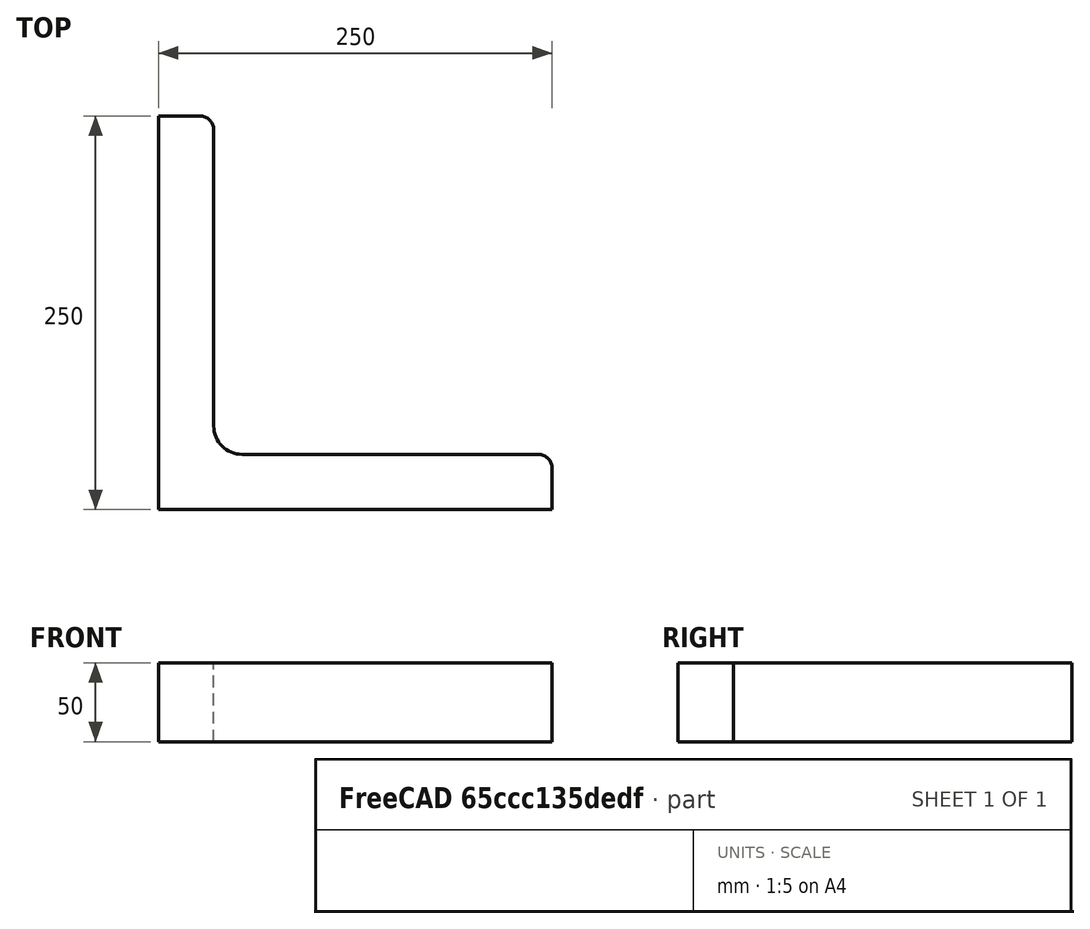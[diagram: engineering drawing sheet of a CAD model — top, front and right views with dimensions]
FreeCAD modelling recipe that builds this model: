
FCSTD DOCUMENT  (FreeCAD 0.15R4671 (Git))
Label: Angle Bar L250x250x35 EN10056 S235JR
License: All rights reserved
LicenseURL: http://en.wikipedia.org/wiki/All_rights_reserved
objects: Sketcher::SketchObject×1, Part::Extrusion×1
note: 2 computed .brp shape members not serialized (recipe doc carries the construction recipe); baked Part::Feature solids carry a one-line shape summary decoded from their .brp

FEATURE [Sketcher::SketchObject] Sketch
  sketch-geometry (9):
    g0: LineSegment StartX=0 StartY=0 StartZ=0 EndX=250 EndY=0 EndZ=0
    g1: LineSegment StartX=250 StartY=0 StartZ=0 EndX=250 EndY=26 EndZ=0
    g2: LineSegment StartX=241 StartY=35 StartZ=0 EndX=53 EndY=35 EndZ=0
    g3: LineSegment StartX=0 StartY=0 StartZ=0 EndX=0 EndY=250 EndZ=0
    g4: LineSegment StartX=0 StartY=250 StartZ=0 EndX=26 EndY=250 EndZ=0
    g5: LineSegment StartX=35 StartY=241 StartZ=0 EndX=35 EndY=53 EndZ=0
    g6: ArcOfCircle CenterX=53 CenterY=53 CenterZ=0 NormalX=0 NormalY=0 NormalZ=1 Radius=18 StartAngle=3.14159 EndAngle=4.71239
    g7: ArcOfCircle CenterX=26 CenterY=241 CenterZ=0 NormalX=0 NormalY=0 NormalZ=1 Radius=9 StartAngle=0 EndAngle=1.5708
    g8: ArcOfCircle CenterX=241 CenterY=26 CenterZ=0 NormalX=0 NormalY=0 NormalZ=1 Radius=9 StartAngle=0 EndAngle=1.5708
  constraints (23):
    c: Coincident(g0,g-1)
    c: Horizontal(g0)
    c: Coincident(g1,g0)
    c: Vertical(g1)
    c: Horizontal(g2)
    c: Coincident(g3,g-1)
    c: Vertical(g3)
    c: Coincident(g4,g3)
    c: Horizontal(g4)
    c: Vertical(g5)
    c: Tangent(g5,g6) = -1.5708
    c: Tangent(g2,g6) = 1.5708
    c: Tangent(g4,g7) = 1.5708
    c: Tangent(g5,g7) = 1.5708
    c: Tangent(g2,g8) = -1.5708
    c: Tangent(g1,g8) = -1.5708
    c: DistanceX(g0) = 250
    c: DistanceY(g3) = 250
    c: DistanceY(g0,g2) = 35
    c: DistanceX(g3,g5) = 35
    c: Radius(g6) = 18
    c: Radius(g8) = 9
    c: Radius(g7) = 9
FEATURE [Part::Extrusion] Extrude  label="Angle Bar L250x250x35 EN10056 S235JR"
  Base = -> Sketch
  Dir = (0,0,50)
  Solid = true
